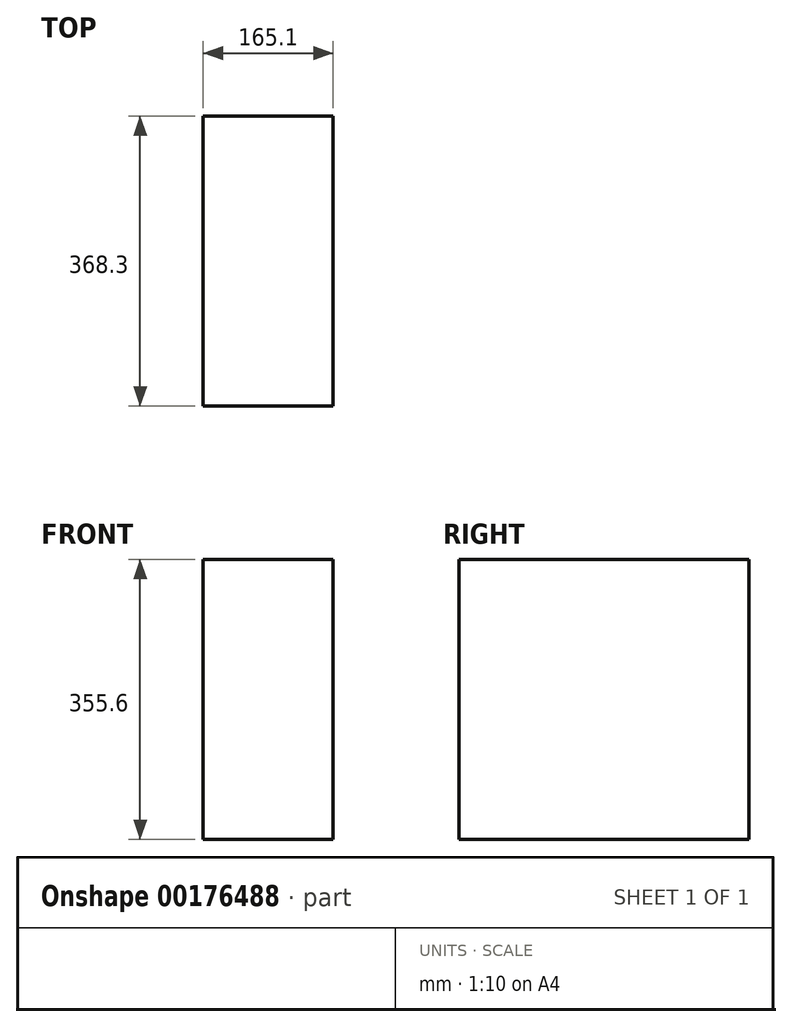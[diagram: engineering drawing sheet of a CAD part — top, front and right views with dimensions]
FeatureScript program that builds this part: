
annotation { "Feature Type Name" : "Feature", "Feature Type Description" : "" }
export const myFeature = defineFeature(function(context is Context, id is Id, definition is map)
    precondition{}
    {
        {
            var Q0;
            Q0=qCreatedBy(makeId("Front.planeOp"),FACE);
            var sketch = newSketch(context, id + "F0", { "sketchPlane" : qUnion([Q0])});
            skLineSegment(sketch, "E0.bottom", {"start": v(82.55, 177.8) * mm, "end": v(-82.55, 177.8) * mm});
            skLineSegment(sketch, "E0.top", {"start": v(82.55, -177.8) * mm, "end": v(-82.55, -177.8) * mm});
            skLineSegment(sketch, "E0.left", {"start": v(82.55, 177.8) * mm, "end": v(82.55, -177.8) * mm});
            skLineSegment(sketch, "E0.right", {"start": v(-82.55, 177.8) * mm, "end": v(-82.55, -177.8) * mm});
            skPoint(sketch, "E0.middle", {"position": v(0, 0) * mm});
            skSolve(sketch);
        }
        {
            var Q0;
            Q0 = qSketchRegion(id + "F0", true);
            extrude(context, id + "F1", {"entities" : qUnion([Q0]), "endBound" : BoundingType.SYMMETRIC, "depth" : 368.3 * mm});
        }
    });
